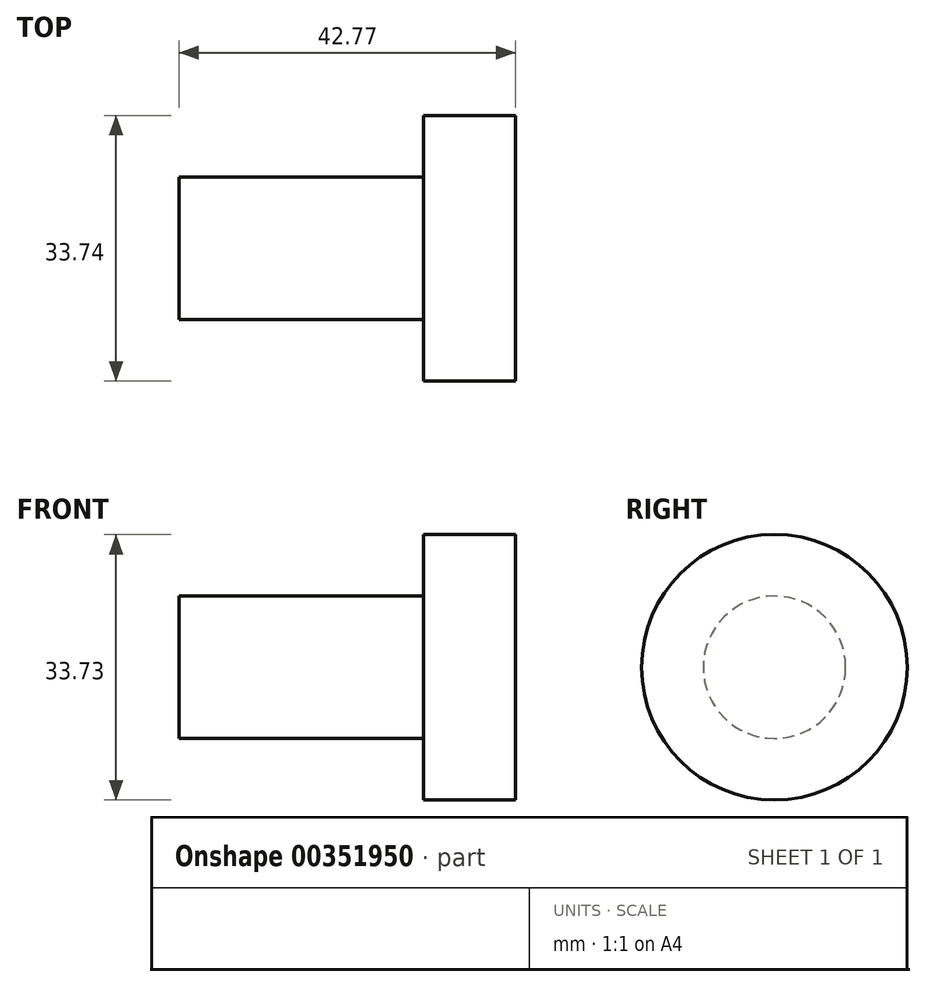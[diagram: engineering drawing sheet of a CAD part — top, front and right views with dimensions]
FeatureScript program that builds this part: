
annotation { "Feature Type Name" : "Feature", "Feature Type Description" : "" }
export const myFeature = defineFeature(function(context is Context, id is Id, definition is map)
    precondition{}
    {
        {
            var Q0;
            Q0=qCreatedBy(makeId("Front.planeOp"),FACE);
            var sketch = newSketch(context, id + "F0", { "sketchPlane" : qUnion([Q0])});
            skLineSegment(sketch, "E0.bottom", {"start": v(-31.04, -1.42) * mm, "end": v(11.73, -1.42) * mm});
            skLineSegment(sketch, "E0.top", {"start": v(-31.04, -10.46) * mm, "end": v(11.73, -10.46) * mm});
            skLineSegment(sketch, "E0.left", {"start": v(-31.04, -1.42) * mm, "end": v(-31.04, -10.46) * mm});
            skLineSegment(sketch, "E0.right", {"start": v(11.73, -1.42) * mm, "end": v(11.73, -10.46) * mm});
            skLineSegment(sketch, "E1.bottom", {"start": v(11.73, -1.42) * mm, "end": v(0, -1.42) * mm});
            skLineSegment(sketch, "E2.bottom", {"start": v(0, -1.42) * mm, "end": v(-9.98, -1.42) * mm});
            skLineSegment(sketch, "E2.top", {"start": v(0, 6.4) * mm, "end": v(-9.98, 6.4) * mm});
            skLineSegment(sketch, "E2.right", {"start": v(-9.98, -1.42) * mm, "end": v(-9.98, 6.4) * mm});
            skLineSegment(sketch, "E3.bottom", {"start": v(0, 6.4) * mm, "end": v(-3.91, 6.4) * mm});
            skLineSegment(sketch, "E4.bottom", {"start": v(0, 6.4) * mm, "end": v(11.73, 6.4) * mm});
            skLineSegment(sketch, "E4.top", {"start": v(0, -1.42) * mm, "end": v(11.73, -1.42) * mm});
            skLineSegment(sketch, "E4.left", {"start": v(0, 6.4) * mm, "end": v(0, -1.42) * mm});
            skLineSegment(sketch, "E4.right", {"start": v(11.73, 6.4) * mm, "end": v(11.73, -1.42) * mm});
            skLineSegment(sketch, "E5.top", {"start": v(0, 25.48) * mm, "end": v(-3.91, 25.48) * mm});
            skLineSegment(sketch, "E5.left", {"start": v(0, 6.4) * mm, "end": v(0, 25.48) * mm});
            skLineSegment(sketch, "E5.right", {"start": v(-3.91, 6.4) * mm, "end": v(-3.91, 25.48) * mm});
            skSolve(sketch);
        }
        {
            var Q0;
            Q0=makeQuery(id+"F0.imprint","IMPRINT",FACE,{"disambiguationData":[TD([[makeQuery(id+"F0.imprint","IMPRINT",EDGE,{"derivedFrom":sQuery(id+"F0.wireOp",EDGE,"E3.bottom")}),-1.0]])]});
            var Q1;
            Q1=makeQuery(id+"F0.imprint","IMPRINT",FACE,{"disambiguationData":[TD([[makeQuery(id+"F0.imprint","IMPRINT",EDGE,{"derivedFrom":sQuery(id+"F0.wireOp",EDGE,"E2.bottom")}),-1.0]])]});
            var Q2;
            Q2=makeQuery(id+"F0.imprint","IMPRINT",FACE,{"disambiguationData":[TD([[makeQuery(id+"F0.imprint","IMPRINT",EDGE,{"derivedFrom":sQuery(id+"F0.wireOp",EDGE,"E4.bottom")}),-1.0]])]});
            var Q3;
            Q3=makeQuery(id+"F0.imprint","IMPRINT",FACE,{"disambiguationData":[TD([[makeQuery(id+"F0.imprint","IMPRINT",EDGE,{"derivedFrom":sQuery(id+"F0.wireOp",EDGE,"E0.bottom")}),-1.0]])]});
            var Q4;
            Q4=sQuery(id+"F0.wireOp",EDGE,"E0.top");
            revolve(context, id + "F1", {"entities" : qUnion([Q0, Q1, Q2, Q3]), "axis" : qUnion([Q4]), "revolveType" : RevolveType.FULL});
        }
    });
